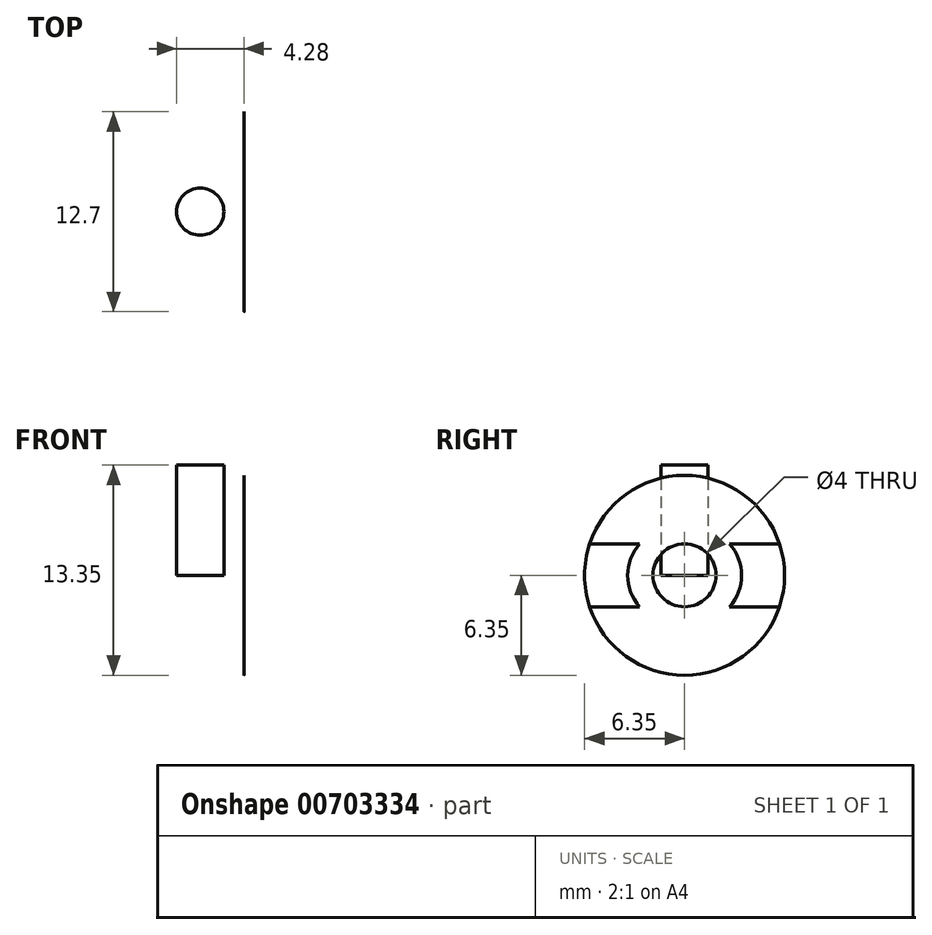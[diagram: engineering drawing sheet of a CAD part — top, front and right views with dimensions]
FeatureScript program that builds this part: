
annotation { "Feature Type Name" : "Feature", "Feature Type Description" : "" }
export const myFeature = defineFeature(function(context is Context, id is Id, definition is map)
    precondition{}
    {
        {
            var Q0;
            Q0=qCreatedBy(makeId("Right.planeOp"),FACE);
            var sketch = newSketch(context, id + "F0", { "sketchPlane" : qUnion([Q0])});
            skCircle(sketch, "E0", {"center": v(0, 0) * mm, "radius": 6.35 * mm});
            skCircle(sketch, "E1", {"center": v(0, 0) * mm, "radius": 2 * mm});
            skLineSegment(sketch, "E2", {"start": v(-6.03, 2) * mm, "end": v(-2.85, 2) * mm});
            skLineSegment(sketch, "E3", {"start": v(-6.03, -2) * mm, "end": v(-2.85, -2) * mm});
            skLineSegment(sketch, "E4", {"start": v(6.03, 2) * mm, "end": v(2.85, 2) * mm});
            skLineSegment(sketch, "E5", {"start": v(6.03, -2) * mm, "end": v(2.85, -2) * mm});
            skArc(sketch, "E6", {"start": v(-2.85, 2) * mm, "mid": v(-3.62, 0) * mm, "end": v(-2.85, -2) * mm});
            skArc(sketch, "E7", {"start": v(2.85, -2) * mm, "mid": v(3.62, 0) * mm, "end": v(2.85, 2) * mm});
            skSolve(sketch);
        }
        {
            var Q0;
            Q0=makeQuery(id+"F0.imprint","IMPRINT",FACE,{"disambiguationData":[TD([[makeQuery(id+"F0.imprint","IMPRINT",EDGE,{"derivedFrom":sQuery(id+"F0.wireOp",EDGE,"E1")}),-1.0]])]});
            var Q1;
            {var subQ0=sQuery(id+"F0.wireOp",EDGE,"E2");Q1=makeQuery(id+"F0.imprint","IMPRINT",FACE,{"disambiguationData":[TD([[makeQuery(id+"F0.imprint","IMPRINT",EDGE,{"derivedFrom":subQ0}),-1.0]])]});}
            var Q2;
            {var subQ0=sQuery(id+"F0.wireOp",EDGE,"E4");Q2=makeQuery(id+"F0.imprint","IMPRINT",FACE,{"disambiguationData":[TD([[makeQuery(id+"F0.imprint","IMPRINT",EDGE,{"derivedFrom":subQ0}),1.0]])]});}
            extrude(context, id + "F1", {"entities" : qUnion([Q0, Q1, Q2]), "depth" : -7 / 812.8 * mm, "offsetDistance" : 25 * mm});
        }
        {
            var Q0;
            {var subQ0=sQuery(id+"F0.wireOp",EDGE,"E2");Q0=makeQuery(id+"F0.imprint","IMPRINT",FACE,{"disambiguationData":[TD([[makeQuery(id+"F0.imprint","IMPRINT",EDGE,{"derivedFrom":subQ0}),-1.0]])]});}
            var Q1;
            {var subQ0=sQuery(id+"F0.wireOp",EDGE,"E4");Q1=makeQuery(id+"F0.imprint","IMPRINT",FACE,{"disambiguationData":[TD([[makeQuery(id+"F0.imprint","IMPRINT",EDGE,{"derivedFrom":subQ0}),1.0]])]});}
            extrude(context, id + "F2", {"entities" : qUnion([Q0, Q1]), "operationType" : NewBodyOperationType.ADD, "depth" : 5 / 1625.6 * mm, "offsetDistance" : 25 * mm});
        }
        {
            var Q0;
            Q0=qCreatedBy(makeId("Top.planeOp"),FACE);
            var sketch = newSketch(context, id + "F3", { "sketchPlane" : qUnion([Q0])});
            skCircle(sketch, "E8", {"center": v(-2.78, 0) * mm, "radius": 1.5 * mm});
            skSolve(sketch);
        }
        {
            var Q0;
            Q0=makeQuery(id+"F3.imprint","IMPRINT",FACE,{"disambiguationData":[TD([[makeQuery(id+"F3.imprint","IMPRINT",EDGE,{"derivedFrom":sQuery(id+"F3.wireOp",EDGE,"E8")}),1.0]])]});
            var Q1;
            Q1 = qConstructionFilter(qBodyType(qCreatedBy(id + "F3" ,EDGE), BodyType.WIRE), ConstructionObject.NO);
            extrude(context, id + "F4", {"entities" : qUnion([Q0]), "surfaceEntities" : qUnion([Q1]), "depth" : 7 * mm, "offsetDistance" : 25 * mm});
        }
    });
